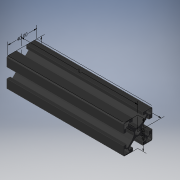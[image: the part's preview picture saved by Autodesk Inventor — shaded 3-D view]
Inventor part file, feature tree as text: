
AUTODESK INVENTOR PART (.ipt)
format: ipt  version: 2019 (Build 230136000, 136)  size: 273,408 bytes
history: native  units: mm
features: other x125, extrude x1, sketch x1
ambient origin geometry x8: Origin, YZ Plane, XZ Plane, XY Plane, X Axis, Y Axis, Z Axis, Center Point
bodies: Solid1 (feature_tree)
feature tree (127):
  other  "Annotations"
  extrude  "Extrusion1"  [1 undecoded]
  other  "CS_ANBAU_HINTEN_LINKS_XY"
  other  "CS_ANBAU_HINTEN_LINKS_YZ"
  other  "CS_ANBAU_HINTEN_LINKS_ZX"
  other  "CS_ANBAU_HINTEN_LINKS_X"
  other  "CS_ANBAU_HINTEN_LINKS_Y"
  other  "CS_ANBAU_HINTEN_LINKS_Z"
  other  "CS_ANBAU_HINTEN_LINKS_Center"
  other  "CS_ANBAU_HINTEN_OBEN_XY"
  other  "CS_ANBAU_HINTEN_OBEN_YZ"
  other  "CS_ANBAU_HINTEN_OBEN_ZX"
  other  "CS_ANBAU_HINTEN_OBEN_X"
  other  "CS_ANBAU_HINTEN_OBEN_Y"
  other  "CS_ANBAU_HINTEN_OBEN_Z"
  other  "CS_ANBAU_HINTEN_OBEN_Center"
  other  "CS_ANBAU_HINTEN_RECHTS_XY"
  other  "CS_ANBAU_HINTEN_RECHTS_YZ"
  other  "CS_ANBAU_HINTEN_RECHTS_ZX"
  other  "CS_ANBAU_HINTEN_RECHTS_X"
  other  "CS_ANBAU_HINTEN_RECHTS_Y"
  other  "CS_ANBAU_HINTEN_RECHTS_Z"
  other  "CS_ANBAU_HINTEN_RECHTS_Center"
  other  "CS_ANBAU_HINTEN_UNTEN_XY"
  other  "CS_ANBAU_HINTEN_UNTEN_YZ"
  other  "CS_ANBAU_HINTEN_UNTEN_ZX"
  other  "CS_ANBAU_HINTEN_UNTEN_X"
  other  "CS_ANBAU_HINTEN_UNTEN_Y"
  other  "CS_ANBAU_HINTEN_UNTEN_Z"
  other  "CS_ANBAU_HINTEN_UNTEN_Center"
  other  "CS_ANBAU_QUER_XY"
  other  "CS_ANBAU_QUER_YZ"
  other  "CS_ANBAU_QUER_ZX"
  other  "CS_ANBAU_QUER_X"
  other  "CS_ANBAU_QUER_Y"
  other  "CS_ANBAU_QUER_Z"
  other  "CS_ANBAU_QUER_Center"
  other  "CS_ANBAU_QUER_1_XY"
  other  "CS_ANBAU_QUER_1_YZ"
  other  "CS_ANBAU_QUER_1_ZX"
  other  "CS_ANBAU_QUER_1_X"
  other  "CS_ANBAU_QUER_1_Y"
  other  "CS_ANBAU_QUER_1_Z"
  other  "CS_ANBAU_QUER_1_Center"
  other  "CS_ANBAU_VORNE_LINKS_XY"
  other  "CS_ANBAU_VORNE_LINKS_YZ"
  other  "CS_ANBAU_VORNE_LINKS_ZX"
  other  "CS_ANBAU_VORNE_LINKS_X"
  other  "CS_ANBAU_VORNE_LINKS_Y"
  other  "CS_ANBAU_VORNE_LINKS_Z"
  other  "CS_ANBAU_VORNE_LINKS_Center"
  other  "CS_ANBAU_VORNE_OBEN_XY"
  other  "CS_ANBAU_VORNE_OBEN_YZ"
  other  "CS_ANBAU_VORNE_OBEN_ZX"
  other  "CS_ANBAU_VORNE_OBEN_X"
  other  "CS_ANBAU_VORNE_OBEN_Y"
  other  "CS_ANBAU_VORNE_OBEN_Z"
  other  "CS_ANBAU_VORNE_OBEN_Center"
  other  "CS_ANBAU_VORNE_RECHTS_XY"
  other  "CS_ANBAU_VORNE_RECHTS_YZ"
  other  "CS_ANBAU_VORNE_RECHTS_ZX"
  other  "CS_ANBAU_VORNE_RECHTS_X"
  other  "CS_ANBAU_VORNE_RECHTS_Y"
  other  "CS_ANBAU_VORNE_RECHTS_Z"
  other  "CS_ANBAU_VORNE_RECHTS_Center"
  other  "CS_ANBAU_VORNE_UNTEN_XY"
  other  "CS_ANBAU_VORNE_UNTEN_YZ"
  other  "CS_ANBAU_VORNE_UNTEN_ZX"
  other  "CS_ANBAU_VORNE_UNTEN_X"
  other  "CS_ANBAU_VORNE_UNTEN_Y"
  other  "CS_ANBAU_VORNE_UNTEN_Z"
  other  "CS_ANBAU_VORNE_UNTEN_Center"
  other  "p1_XY"
  other  "p1_YZ"
  other  "p1_ZX"
  other  "p1_X"
  other  "p1_Y"
  other  "p1_Z"
  other  "p1_Center"
  other  "p2_XY"
  other  "p2_YZ"
  other  "p2_ZX"
  other  "p2_X"
  other  "p2_Y"
  other  "p2_Z"
  other  "p2_Center"
  other  "p3_XY"
  other  "p3_YZ"
  other  "p3_ZX"
  other  "p3_X"
  other  "p3_Y"
  other  "p3_Z"
  other  "p3_Center"
  other  "p4_XY"
  other  "p4_YZ"
  other  "p4_ZX"
  other  "p4_X"
  other  "p4_Y"
  other  "p4_Z"
  other  "p4_Center"
  other  "p5_XY"
  other  "p5_YZ"
  other  "p5_ZX"
  other  "p5_X"
  other  "p5_Y"
  other  "p5_Z"
  other  "p5_Center"
  other  "pm1_XY"
  other  "pm1_YZ"
  other  "pm1_ZX"
  other  "pm1_X"
  other  "pm1_Y"
  other  "pm1_Z"
  other  "pm1_Center"
  other  "pm2_XY"
  other  "pm2_YZ"
  other  "pm2_ZX"
  other  "pm2_X"
  other  "pm2_Y"
  other  "pm2_Z"
  other  "pm2_Center"
  sketch  "Skizze_1"  dims[d0=161.0mm d1=0.0mm d2=0.0mm d3=0.0mm d4=0.0mm d5=0.0mm d6=0.0mm d10=161.0mm d11=161.0mm d7=40.0mm d8=40.0mm d9=40.0mm]
  other  "Linear Dimension 1"
  other  "Linear Dimension 2"
  other  "Linear Dimension 3"
  other  "Linear Dimension 4"
  other  "Linear Dimension 5"
note: 1 required parameter value undecoded (feature->parameter linkage not recoverable at this tier; creation-order binding heuristic only, values carry confidence <= 0.55)
